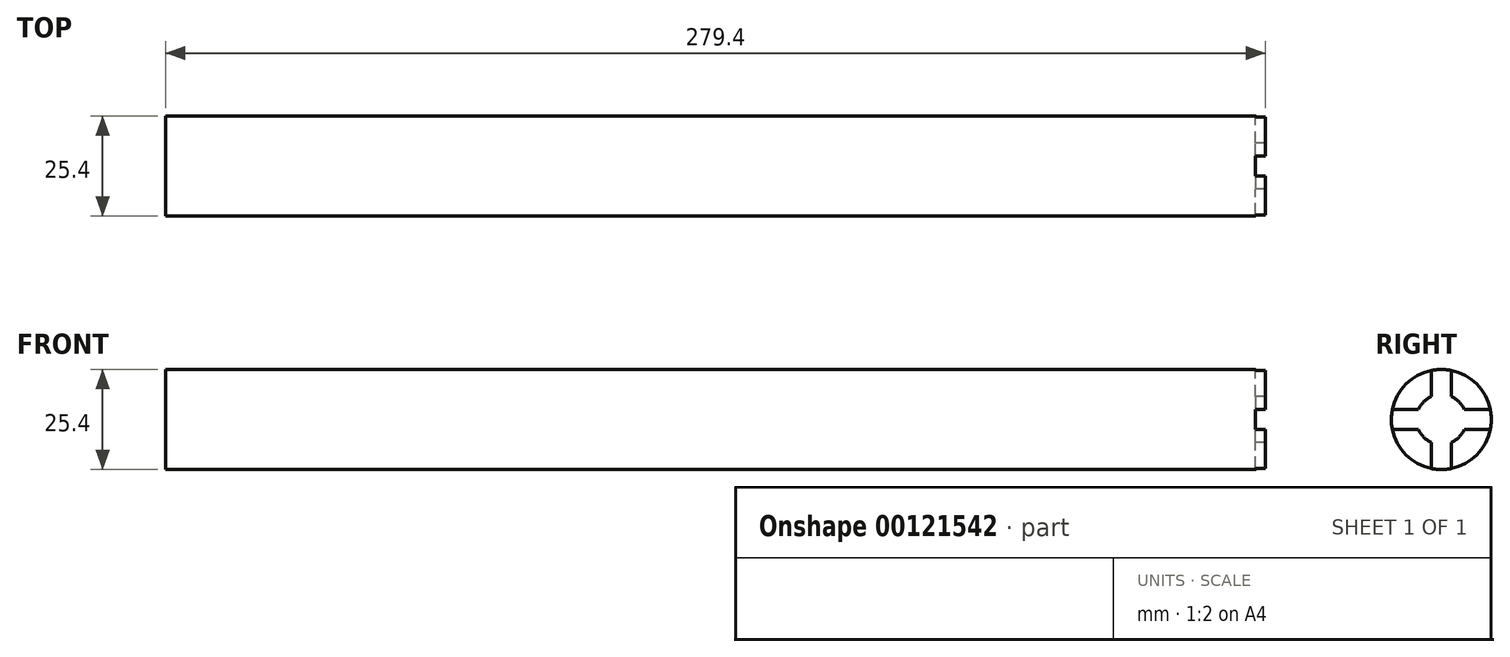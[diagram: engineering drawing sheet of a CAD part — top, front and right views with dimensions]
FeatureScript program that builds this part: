
annotation { "Feature Type Name" : "Feature", "Feature Type Description" : "" }
export const myFeature = defineFeature(function(context is Context, id is Id, definition is map)
    precondition{}
    {
        {
            var Q0;
            Q0=qCreatedBy(makeId("Front.planeOp"),FACE);
            var sketch = newSketch(context, id + "F0", { "sketchPlane" : qUnion([Q0])});
            skLineSegment(sketch, "E0", {"start": v(0, 12.7) * mm, "end": v(0, 0) * mm});
            skLineSegment(sketch, "E1", {"start": v(0, 12.7) * mm, "end": v(39.2, 12.7) * mm});
            skLineSegment(sketch, "E2", {"start": v(39.2, 12.7) * mm, "end": v(39.2, 0) * mm});
            skLineSegment(sketch, "E3", {"start": v(39.2, 0) * mm, "end": v(0, 0) * mm});
            skLineSegment(sketch, "E4", {"start": v(39.2, 12.7) * mm, "end": v(279.4, 12.7) * mm});
            skLineSegment(sketch, "E5", {"start": v(39.2, 0) * mm, "end": v(276.86, 0) * mm});
            skLineSegment(sketch, "E6", {"start": v(251.31, 12.7) * mm, "end": v(251.31, 0) * mm});
            skLineSegment(sketch, "E7", {"start": v(279.4, 12.7) * mm, "end": v(279.4, 6.35) * mm});
            skLineSegment(sketch, "E8", {"start": v(279.4, 6.35) * mm, "end": v(276.86, 6.35) * mm});
            skLineSegment(sketch, "E9", {"start": v(276.86, 6.35) * mm, "end": v(276.86, 0) * mm});
            skLineSegment(sketch, "E10", {"start": v(0, 0) * mm, "end": v(293.71, 0) * mm, "construction": true});
            skSolve(sketch);
        }
        {
            var Q0;
            Q0 = qSketchRegion(id + "F0", true);
            var Q1;
            Q1=sQuery(id+"F0.wireOp",EDGE,"E10");
            revolve(context, id + "F1", {"entities" : qUnion([Q0]), "axis" : qUnion([Q1]), "revolveType" : RevolveType.FULL});
        }
        {
            var Q0;
            Q0=makeQuery(id+"F1.opRevolve","SWEPT_FACE",FACE,{"disambiguationData":[OSD([sQuery(id+"F0.wireOp",EDGE,"E7")])]});
            var sketch = newSketch(context, id + "F2", { "sketchPlane" : qUnion([Q0])});
            skSolve(sketch);
        }
        {
            var Q0;
            {var subQ0=sQuery(id+"F0.wireOp",EDGE,"E7");Q0=makeQuery(id+"F2.imprint","IMPRINT",FACE,{"disambiguationData":[TD([[makeQuery(id+"F2.imprint","IMPRINT",EDGE,{"derivedFrom":makeQuery(id+"F1.opRevolve","SWEPT_EDGE",EDGE,{"disambiguationData":[OSD([sQuery(id+"F0.wireOp",EDGE,"E4"),subQ0])]})}),-1.0]])]});}
            var sketch = newSketch(context, id + "F3", { "sketchPlane" : qUnion([Q0])});
            skLineSegment(sketch, "E11", {"start": v(0, 34.12) * mm, "end": v(0, -29.27) * mm, "construction": true});
            skLineSegment(sketch, "E12.bottom", {"start": v(2.54, -15.8) * mm, "end": v(-2.54, -15.8) * mm});
            skLineSegment(sketch, "E12.top", {"start": v(2.54, 15.8) * mm, "end": v(-2.54, 15.8) * mm});
            skLineSegment(sketch, "E12.left", {"start": v(2.54, -15.8) * mm, "end": v(2.54, 15.8) * mm});
            skLineSegment(sketch, "E12.right", {"start": v(-2.54, -15.8) * mm, "end": v(-2.54, 15.8) * mm});
            skPoint(sketch, "E12.middle", {"position": v(0, 0) * mm});
            skLineSegment(sketch, "E13.bottom", {"start": v(-21.57, -2.54) * mm, "end": v(21.57, -2.54) * mm});
            skLineSegment(sketch, "E13.top", {"start": v(-21.57, 2.54) * mm, "end": v(21.57, 2.54) * mm});
            skLineSegment(sketch, "E13.left", {"start": v(-21.57, -2.54) * mm, "end": v(-21.57, 2.54) * mm});
            skLineSegment(sketch, "E13.right", {"start": v(21.57, -2.54) * mm, "end": v(21.57, 2.54) * mm});
            skSolve(sketch);
        }
        {
            var Q0;
            Q0 = qSketchRegion(id + "F3", true);
            extrude(context, id + "F4", {"entities" : qUnion([Q0]), "operationType" : NewBodyOperationType.REMOVE, "oppositeDirection" : true, "depth" : 2.54 * mm});
        }
        {
            var Q0;
            Q0 = qSketchRegion(id + "F3", true);
            extrude(context, id + "F5", {"entities" : qUnion([Q0]), "operationType" : NewBodyOperationType.REMOVE, "oppositeDirection" : true, "depth" : 2.54 * mm});
        }
    });
